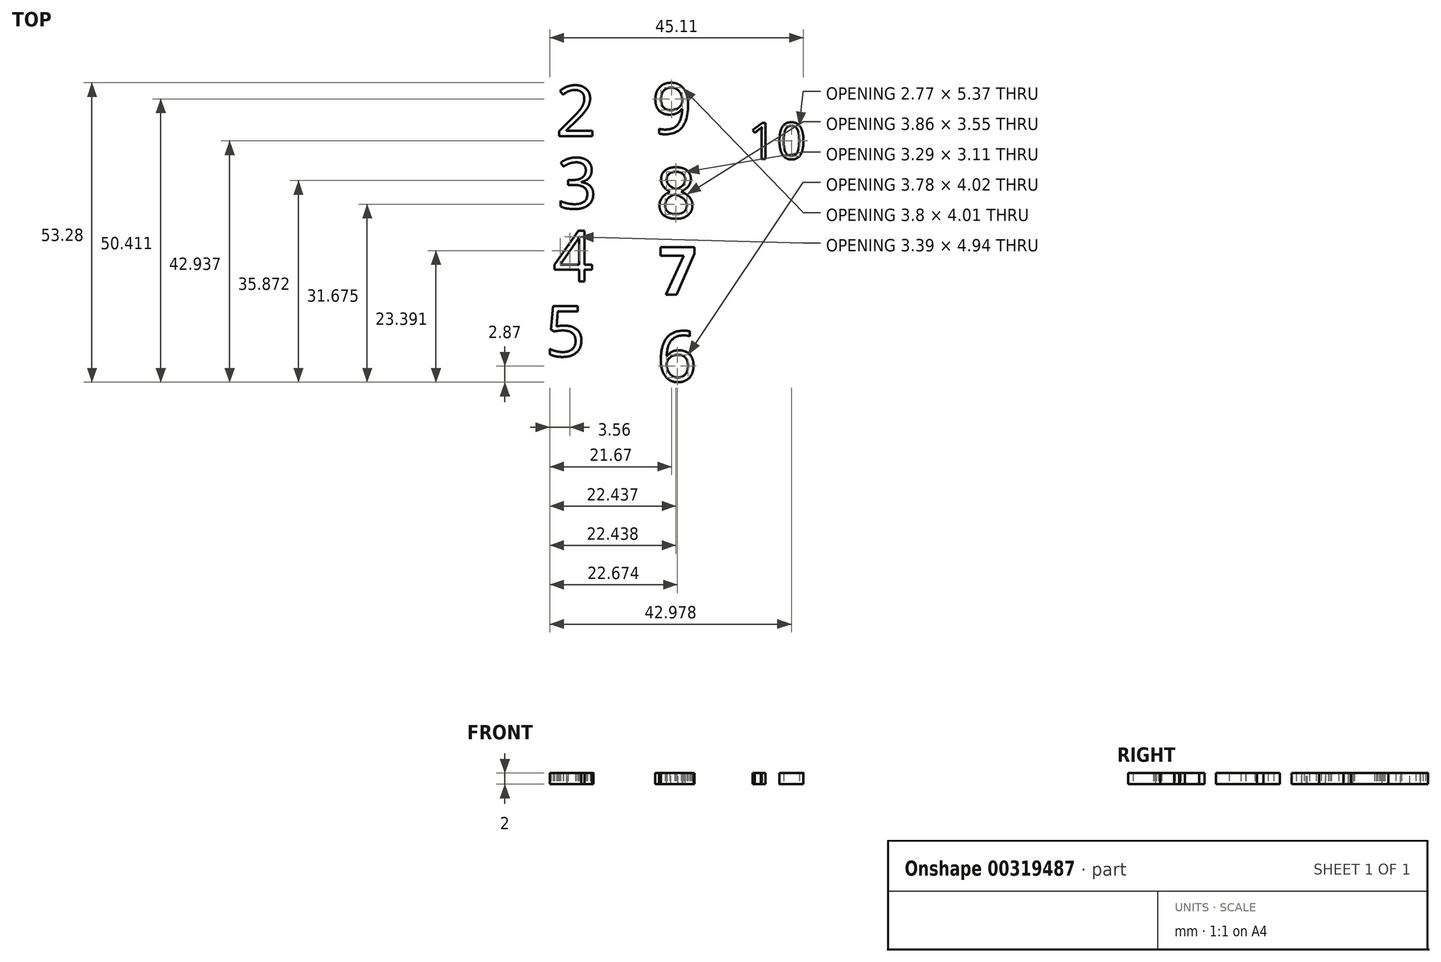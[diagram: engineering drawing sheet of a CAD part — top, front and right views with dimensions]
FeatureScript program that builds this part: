
annotation { "Feature Type Name" : "Feature", "Feature Type Description" : "" }
export const myFeature = defineFeature(function(context is Context, id is Id, definition is map)
    precondition{}
    {
        {
            var Q0;
            Q0=qCreatedBy(makeId("Top.planeOp"),FACE);
            var sketch = newSketch(context, id + "F0", { "sketchPlane" : qUnion([Q0])});
            skText(sketch, "E0", { "text": "2", "fontName": "OpenSans-Regular.ttf"});
            skText(sketch, "E1", { "text": "3", "fontName": "OpenSans-Regular.ttf"});
            skText(sketch, "E2", { "text": "4", "fontName": "OpenSans-Regular.ttf"});
            skText(sketch, "E3", { "text": "5", "fontName": "OpenSans-Regular.ttf"});
            skText(sketch, "E4", { "text": "6", "fontName": "OpenSans-Regular.ttf"});
            skText(sketch, "E5", { "text": "7", "fontName": "OpenSans-Bold.ttf"});
            skText(sketch, "E6", { "text": "8", "fontName": "OpenSans-Regular.ttf"});
            skText(sketch, "E7", { "text": "9", "fontName": "OpenSans-Regular.ttf"});
            skText(sketch, "E8", { "text": "10", "fontName": "OpenSans-Regular.ttf"});
            const initialGuessF0  = {"E0": [-0.0591, 0.05432, 1, 0, 0.009], "E1": [-0.05886, 0.04145, 1, 0, 0.009], "E2": [-0.05958, 0.02847, 1, 0, 0.009], "E3": [-0.06098, 0.01514, 1, 0, 0.009], "E4": [-0.04114, 0.01064, 1, 0, 0.009], "E5": [-0.04082, 0.02613, 1, 0, 0.0085], "E6": [-0.0413, 0.03972, 1, 0, 0.009], "E7": [-0.04205, 0.05475, 1, 0, 0.009], "E8": [-0.02493, 0.05023, 1, 0, 0.0065]};
            skSetInitialGuess(sketch, initialGuessF0);
            skSolve(sketch);
        }
        {
            var Q0;
            Q0=makeQuery(id+"F0.imprint","IMPRINT",FACE,{"disambiguationData":[TD([[makeQuery(id+"F0.imprint","IMPRINT",EDGE,{"derivedFrom":sQuery(id+"F0.wireOp",EDGE,"573c7ff4-228d-4a1a-a689-163ace67b3cf.sketch_text.stroke-0")}),-1.0]])]});
            var Q1;
            Q1=makeQuery(id+"F0.imprint","IMPRINT",FACE,{"disambiguationData":[TD([[makeQuery(id+"F0.imprint","IMPRINT",EDGE,{"derivedFrom":sQuery(id+"F0.wireOp",EDGE,"6156cb96-52c7-45c1-a00d-06670b02b893.sketch_text.stroke-0")}),-1.0]])]});
            var Q2;
            Q2=makeQuery(id+"F0.imprint","IMPRINT",FACE,{"disambiguationData":[TD([[makeQuery(id+"F0.imprint","IMPRINT",EDGE,{"derivedFrom":sQuery(id+"F0.wireOp",EDGE,"E0.sketch_text.stroke-0")}),-1.0]])]});
            var Q3;
            Q3=makeQuery(id+"F0.imprint","IMPRINT",FACE,{"disambiguationData":[TD([[makeQuery(id+"F0.imprint","IMPRINT",EDGE,{"derivedFrom":sQuery(id+"F0.wireOp",EDGE,"E1.sketch_text.stroke-0")}),-1.0]])]});
            var Q4;
            Q4=makeQuery(id+"F0.imprint","IMPRINT",FACE,{"disambiguationData":[TD([[makeQuery(id+"F0.imprint","IMPRINT",EDGE,{"derivedFrom":sQuery(id+"F0.wireOp",EDGE,"E2.sketch_text.stroke-0")}),-1.0]])]});
            var Q5;
            Q5=makeQuery(id+"F0.imprint","IMPRINT",FACE,{"disambiguationData":[TD([[makeQuery(id+"F0.imprint","IMPRINT",EDGE,{"derivedFrom":sQuery(id+"F0.wireOp",EDGE,"E7.sketch_text.stroke-0")}),-1.0]])]});
            var Q6;
            Q6=makeQuery(id+"F0.imprint","IMPRINT",FACE,{"disambiguationData":[TD([[makeQuery(id+"F0.imprint","IMPRINT",EDGE,{"derivedFrom":sQuery(id+"F0.wireOp",EDGE,"E6.sketch_text.stroke-0")}),-1.0]])]});
            var Q7;
            Q7=makeQuery(id+"F0.imprint","IMPRINT",FACE,{"disambiguationData":[TD([[makeQuery(id+"F0.imprint","IMPRINT",EDGE,{"derivedFrom":sQuery(id+"F0.wireOp",EDGE,"E5.sketch_text.stroke-0")}),-1.0]])]});
            var Q8;
            Q8=makeQuery(id+"F0.imprint","IMPRINT",FACE,{"disambiguationData":[TD([[makeQuery(id+"F0.imprint","IMPRINT",EDGE,{"derivedFrom":sQuery(id+"F0.wireOp",EDGE,"E3.sketch_text.stroke-0")}),-1.0]])]});
            var Q9;
            Q9=makeQuery(id+"F0.imprint","IMPRINT",FACE,{"disambiguationData":[TD([[makeQuery(id+"F0.imprint","IMPRINT",EDGE,{"derivedFrom":sQuery(id+"F0.wireOp",EDGE,"E4.sketch_text.stroke-0")}),-1.0]])]});
            var Q10;
            Q10=makeQuery(id+"F0.imprint","IMPRINT",FACE,{"disambiguationData":[TD([[makeQuery(id+"F0.imprint","IMPRINT",EDGE,{"derivedFrom":sQuery(id+"F0.wireOp",EDGE,"E8.sketch_text.stroke-9")}),-1.0]])]});
            var Q11;
            Q11=makeQuery(id+"F0.imprint","IMPRINT",FACE,{"disambiguationData":[TD([[makeQuery(id+"F0.imprint","IMPRINT",EDGE,{"derivedFrom":sQuery(id+"F0.wireOp",EDGE,"E8.sketch_text.stroke-0")}),-1.0]])]});
            extrude(context, id + "F1", {"entities" : qUnion([Q0, Q1, Q2, Q3, Q4, Q5, Q6, Q7, Q8, Q9, Q10, Q11]), "depth" : 2 * mm});
        }
    });
